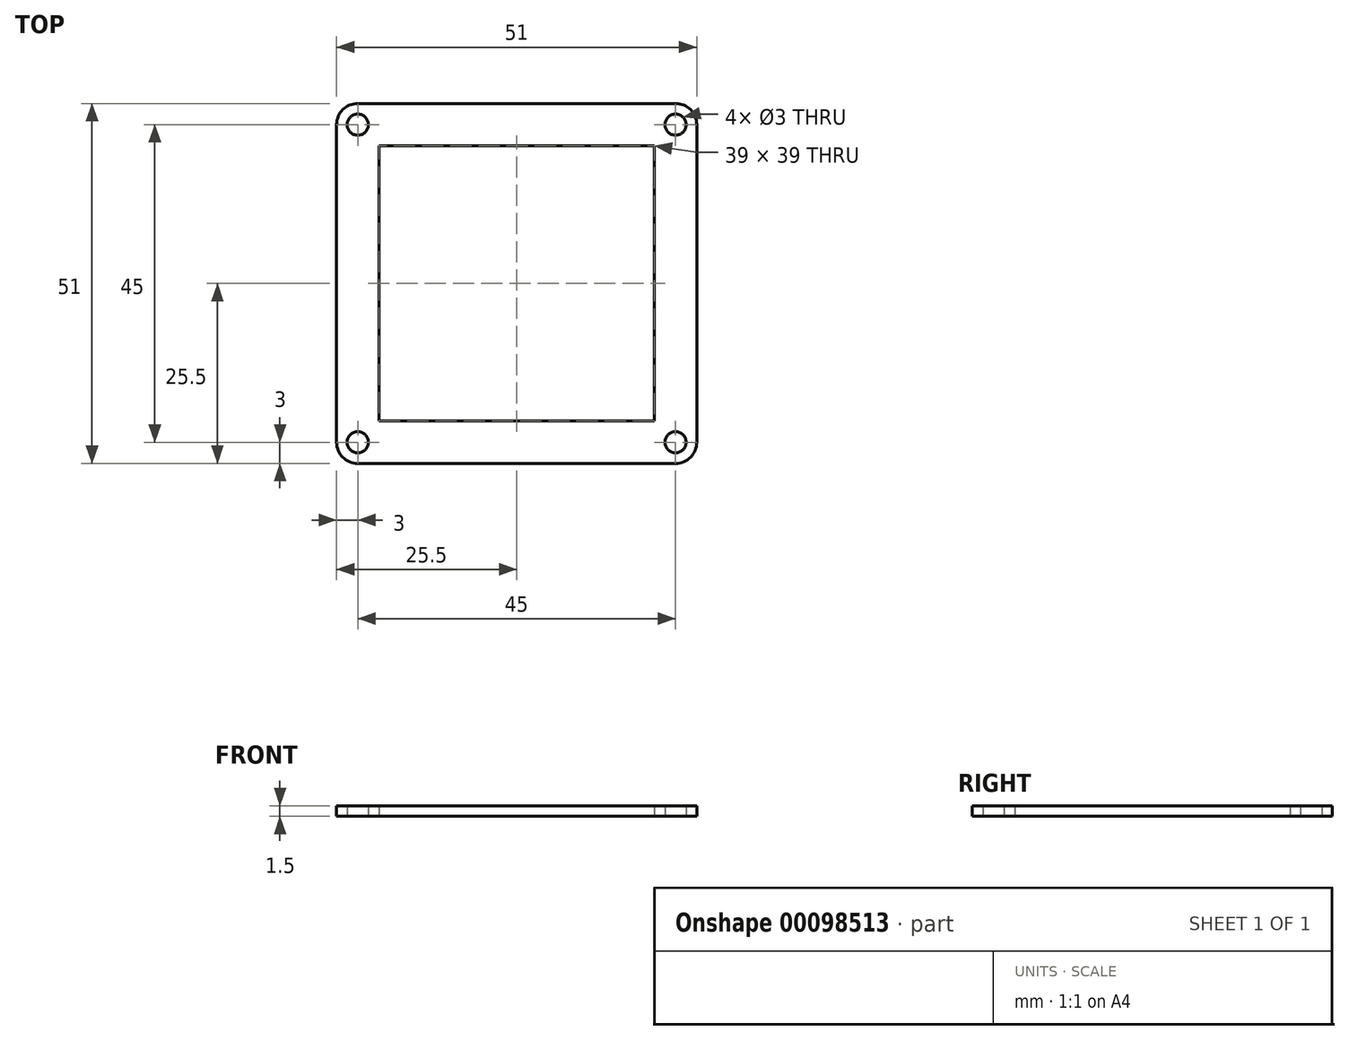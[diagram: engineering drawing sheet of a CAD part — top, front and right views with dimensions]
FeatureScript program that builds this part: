
annotation { "Feature Type Name" : "Feature", "Feature Type Description" : "" }
export const myFeature = defineFeature(function(context is Context, id is Id, definition is map)
    precondition{}
    {
        {
            var Q0;
            Q0=qCreatedBy(makeId("Top.planeOp"),FACE);
            var sketch = newSketch(context, id + "F0", { "sketchPlane" : qUnion([Q0])});
            skLineSegment(sketch, "E0.bottom", {"start": v(22.5, -22.5) * mm, "end": v(-22.5, -22.5) * mm});
            skLineSegment(sketch, "E0.top", {"start": v(22.5, 22.5) * mm, "end": v(-22.5, 22.5) * mm});
            skLineSegment(sketch, "E0.left", {"start": v(22.5, -22.5) * mm, "end": v(22.5, 22.5) * mm});
            skLineSegment(sketch, "E0.right", {"start": v(-22.5, -22.5) * mm, "end": v(-22.5, 22.5) * mm});
            skPoint(sketch, "E0.middle", {"position": v(0, 0) * mm});
            skLineSegment(sketch, "E1.bottom", {"start": v(19.5, 19.5) * mm, "end": v(-19.5, 19.5) * mm});
            skLineSegment(sketch, "E1.top", {"start": v(19.5, -19.5) * mm, "end": v(-19.5, -19.5) * mm});
            skLineSegment(sketch, "E1.left", {"start": v(19.5, 19.5) * mm, "end": v(19.5, -19.5) * mm});
            skLineSegment(sketch, "E1.right", {"start": v(-19.5, 19.5) * mm, "end": v(-19.5, -19.5) * mm});
            skLineSegment(sketch, "E2", {"start": v(19.5, 19.5) * mm, "end": v(22.5, 19.5) * mm});
            skLineSegment(sketch, "E3", {"start": v(19.5, -19.5) * mm, "end": v(19.5, -22.5) * mm});
            skLineSegment(sketch, "E4", {"start": v(-19.5, -19.5) * mm, "end": v(-22.5, -19.5) * mm});
            skLineSegment(sketch, "E5", {"start": v(-19.5, 19.5) * mm, "end": v(-19.5, 22.5) * mm});
            skLineSegment(sketch, "E6.bottom", {"start": v(25.5, 25.5) * mm, "end": v(-25.5, 25.5) * mm});
            skLineSegment(sketch, "E6.top", {"start": v(25.5, -25.5) * mm, "end": v(-25.5, -25.5) * mm});
            skLineSegment(sketch, "E6.left", {"start": v(25.5, 25.5) * mm, "end": v(25.5, -25.5) * mm});
            skLineSegment(sketch, "E6.right", {"start": v(-25.5, 25.5) * mm, "end": v(-25.5, -25.5) * mm});
            skLineSegment(sketch, "E7", {"start": v(-22.5, 22.5) * mm, "end": v(-22.5, 25.5) * mm});
            skLineSegment(sketch, "E8", {"start": v(22.5, 22.5) * mm, "end": v(25.5, 22.5) * mm});
            skCircle(sketch, "E9", {"center": v(-22.5, 22.5) * mm, "radius": 1.5 * mm});
            skCircle(sketch, "E10", {"center": v(22.5, 22.5) * mm, "radius": 1.5 * mm});
            skCircle(sketch, "E11", {"center": v(22.5, -22.5) * mm, "radius": 1.5 * mm});
            skCircle(sketch, "E12", {"center": v(-22.5, -22.5) * mm, "radius": 1.5 * mm});
            skSolve(sketch);
        }
        {
            var Q0;
            Q0 = qSketchRegion(id + "F0", true);
            var Q1;
            Q1=makeQuery(id+"F0.imprint","IMPRINT",FACE,{"disambiguationData":[TD([[makeQuery(id+"F0.imprint","IMPRINT",EDGE,{"derivedFrom":sQuery(id+"F0.wireOp",EDGE,"E1.top")}),1.0]])]});
            var Q2;
            Q2=makeQuery(id+"F0.imprint","IMPRINT",FACE,{"disambiguationData":[TD([[makeQuery(id+"F0.imprint","IMPRINT",EDGE,{"derivedFrom":sQuery(id+"F0.wireOp",EDGE,"E1.left")}),1.0]])]});
            var Q3;
            Q3=makeQuery(id+"F0.imprint","IMPRINT",FACE,{"disambiguationData":[TD([[makeQuery(id+"F0.imprint","IMPRINT",EDGE,{"derivedFrom":sQuery(id+"F0.wireOp",EDGE,"E1.bottom")}),-1.0]])]});
            var Q4;
            Q4=makeQuery(id+"F0.imprint","IMPRINT",FACE,{"disambiguationData":[TD([[makeQuery(id+"F0.imprint","IMPRINT",EDGE,{"derivedFrom":sQuery(id+"F0.wireOp",EDGE,"E1.right")}),-1.0]])]});
            extrude(context, id + "F1", {"entities" : qUnion([Q0, Q1, Q2, Q3, Q4]), "depth" : 1.5 * mm});
        }
        {
            var Q0;
            Q0=makeQuery(id+"F1.opExtrude","SWEPT_EDGE",EDGE,{"disambiguationData":[OSD([sQuery(id+"F0.wireOp",EDGE,"E6.bottom"),sQuery(id+"F0.wireOp",EDGE,"E6.right")])]});
            var Q1;
            Q1=makeQuery(id+"F1.opExtrude","SWEPT_EDGE",EDGE,{"disambiguationData":[OSD([sQuery(id+"F0.wireOp",EDGE,"E6.top"),sQuery(id+"F0.wireOp",EDGE,"E6.left")])]});
            var Q2;
            Q2=makeQuery(id+"F1.opExtrude","SWEPT_EDGE",EDGE,{"disambiguationData":[OSD([sQuery(id+"F0.wireOp",EDGE,"E6.top"),sQuery(id+"F0.wireOp",EDGE,"E6.right")])]});
            var Q3;
            Q3=makeQuery(id+"F1.opExtrude","SWEPT_EDGE",EDGE,{"disambiguationData":[OSD([sQuery(id+"F0.wireOp",EDGE,"E6.bottom"),sQuery(id+"F0.wireOp",EDGE,"E6.left")])]});
            fillet(context, id + "F2", {"entities" : qUnion([Q0, Q1, Q2, Q3]), "radius" : 3 * mm, "tangentPropagation" : true, "allowEdgeOverflow" : false});
        }
    });
